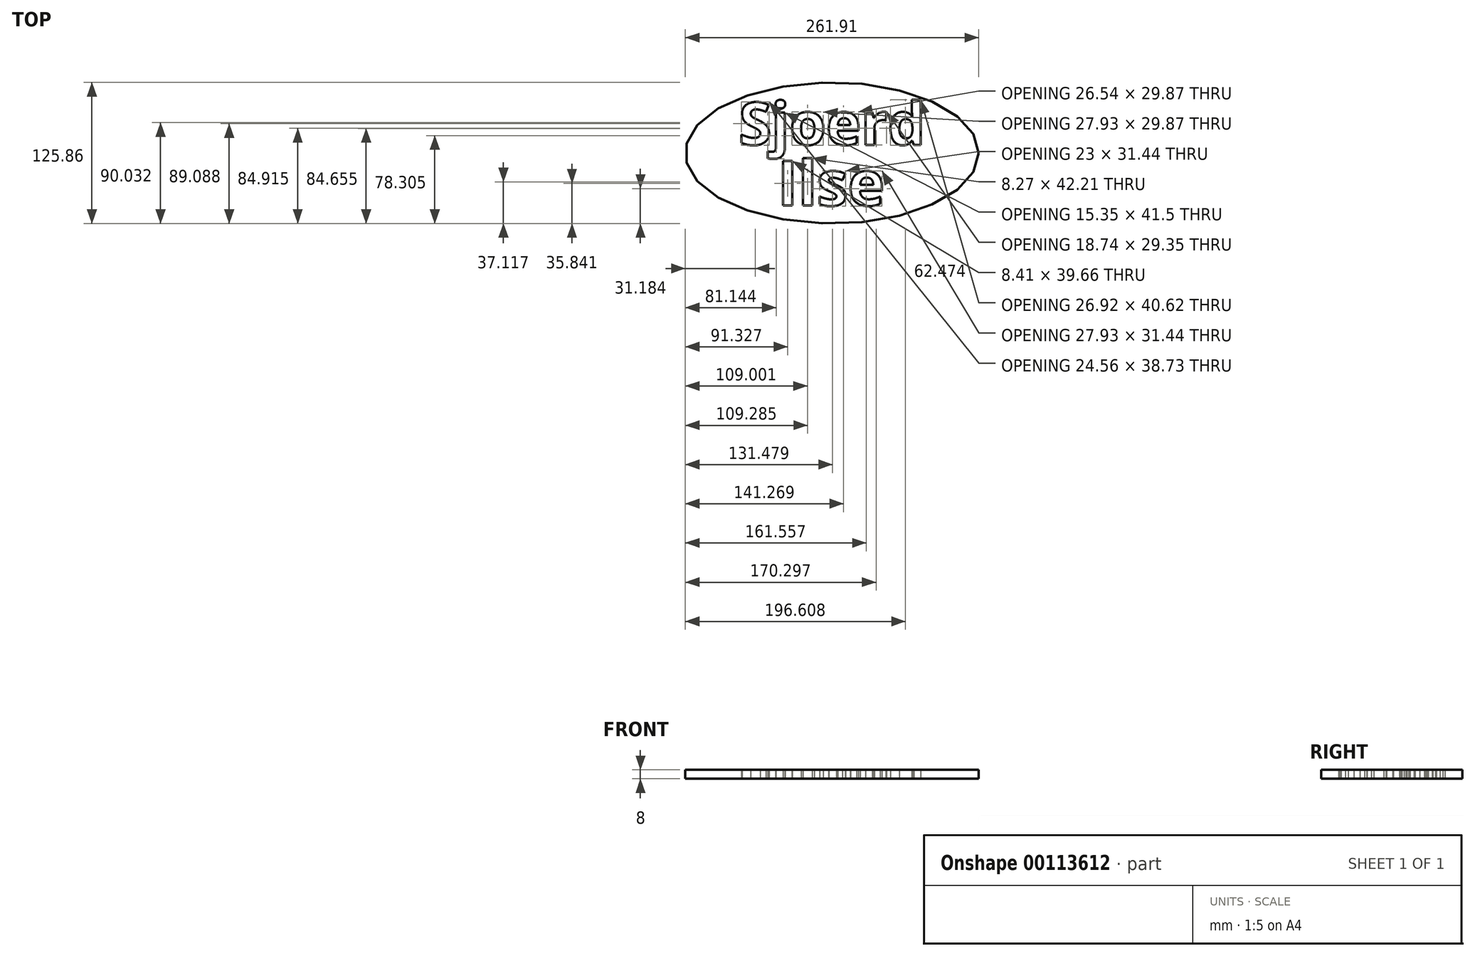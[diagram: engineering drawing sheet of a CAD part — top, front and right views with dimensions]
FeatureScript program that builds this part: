
annotation { "Feature Type Name" : "Feature", "Feature Type Description" : "" }
export const myFeature = defineFeature(function(context is Context, id is Id, definition is map)
    precondition{}
    {
        {
            var Q0;
            Q0=qCreatedBy(makeId("Top.planeOp"),FACE);
            var sketch = newSketch(context, id + "F0", { "sketchPlane" : qUnion([Q0])});
            skText(sketch, "E0", { "text": "Sjoerd", "fontName": "OpenSans-Bold.ttf"});
            skText(sketch, "E1", { "text": "Ilse", "fontName": "OpenSans-Bold.ttf"});
            const initialGuessF0  = {"E0": [-0.08142, 0.02785, 1, 0, 0.038], "E1": [-0.04706, -0.02638, 1, 0, 0.04]};
            skSetInitialGuess(sketch, initialGuessF0);
            skSolve(sketch);
        }
        {
            var Q0;
            Q0=qCreatedBy(makeId("Top.planeOp"),FACE);
            var sketch = newSketch(context, id + "F1", { "sketchPlane" : qUnion([Q0])});
            skEllipse(sketch, "E2", {"center": v(1.76, 20.54) * mm, "majorRadius": 130.96 * mm, "minorRadius": 62.93 * mm, "majorAxis": v(1, 0)});
            skSolve(sketch);
        }
        {
            var Q0;
            Q0 = qSketchRegion(id + "F1", true);
            extrude(context, id + "F2", {"entities" : qUnion([Q0]), "depth" : 8 * mm});
        }
        {
            var Q0;
            Q0 = qSketchRegion(id + "F0", true);
            extrude(context, id + "F3", {"entities" : qUnion([Q0]), "operationType" : NewBodyOperationType.REMOVE, "depth" : 25 * mm});
        }
    });
